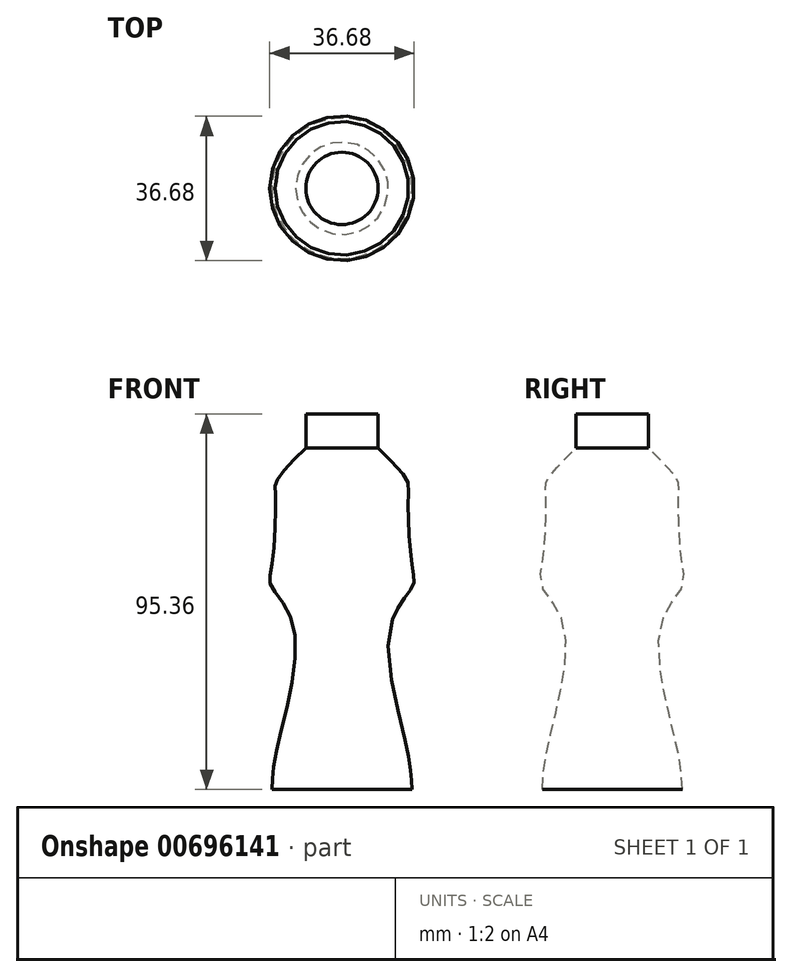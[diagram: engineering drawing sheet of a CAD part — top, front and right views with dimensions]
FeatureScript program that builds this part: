
annotation { "Feature Type Name" : "Feature", "Feature Type Description" : "" }
export const myFeature = defineFeature(function(context is Context, id is Id, definition is map)
    precondition{}
    {
        {
            var Q0;
            Q0=qCreatedBy(makeId("Front.planeOp"),FACE);
            var sketch = newSketch(context, id + "F0", { "sketchPlane" : qUnion([Q0])});
            skLineSegment(sketch, "E0", {"start": v(0, 43.61) * mm, "end": v(0, -51.75) * mm});
            skLineSegment(sketch, "E1", {"start": v(0, 43.61) * mm, "end": v(-9.19, 43.61) * mm});
            skLineSegment(sketch, "E2", {"start": v(-9.19, 43.61) * mm, "end": v(-9.19, 35) * mm});
            skLineSegment(sketch, "E3", {"start": v(0, -51.75) * mm, "end": v(-17.8, -51.75) * mm});
            skFitSpline(sketch, "E4", {"points": [v(-9.19, 35) * mm, v(-16.63, 26.63) * mm, v(-16.86, 23.14) * mm, v(-17.8, 5.23) * mm, v(-18.03, 0) * mm, v(-12.21, -10.58) * mm, v(-16.63, -41.98) * mm, v(-17.8, -51.75) * mm], "startDerivative": vector(-69.96, -69.2) * mm, "endDerivative": vector(-2.18, -59.55) * mm});
            skSolve(sketch);
        }
        {
            var Q0;
            Q0=makeQuery(id+"F0.imprint","IMPRINT",FACE,{"disambiguationData":[TD([[makeQuery(id+"F0.imprint","IMPRINT",EDGE,{"derivedFrom":sQuery(id+"F0.wireOp",EDGE,"E0")}),-1.0]])]});
            var Q1;
            Q1=sQuery(id+"F0.wireOp",EDGE,"E0");
            revolve(context, id + "F1", {"entities" : qUnion([Q0]), "axis" : qUnion([Q1]), "revolveType" : RevolveType.SYMMETRIC, "oppositeDirection" : true, "angle" : 360 * degree});
        }
    });
